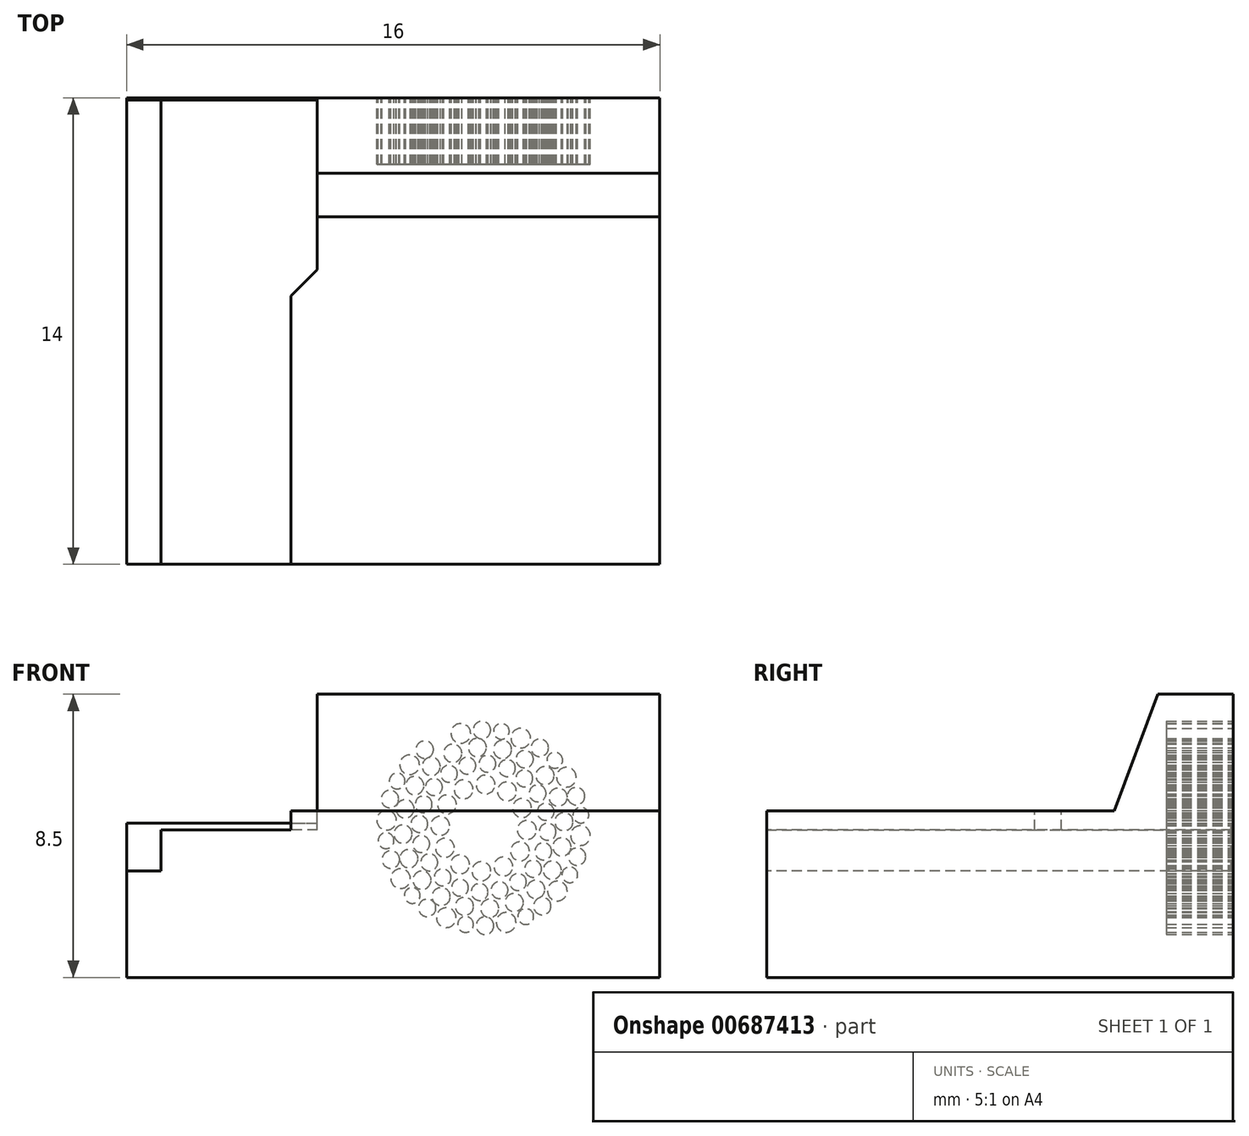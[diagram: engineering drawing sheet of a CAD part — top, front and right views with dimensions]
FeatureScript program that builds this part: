
annotation { "Feature Type Name" : "Feature", "Feature Type Description" : "" }
export const myFeature = defineFeature(function(context is Context, id is Id, definition is map)
    precondition{}
    {
        {
            var Q0;
            Q0=qCreatedBy(makeId("Top.planeOp"),FACE);
            var sketch = newSketch(context, id + "F0", { "sketchPlane" : qUnion([Q0])});
            skLineSegment(sketch, "E0.bottom", {"start": v(-4.9, 18.95) * mm, "end": v(-20.9, 18.95) * mm});
            skLineSegment(sketch, "E0.top", {"start": v(-4.9, 4.95) * mm, "end": v(-20.9, 4.95) * mm});
            skLineSegment(sketch, "E0.left", {"start": v(-4.9, 18.95) * mm, "end": v(-4.9, 4.95) * mm});
            skLineSegment(sketch, "E0.right", {"start": v(-20.9, 18.95) * mm, "end": v(-20.9, 4.95) * mm});
            skSolve(sketch);
        }
        {
            var Q0;
            Q0=makeQuery(id+"F0.imprint","IMPRINT",FACE,{"disambiguationData":[TD([[makeQuery(id+"F0.imprint","IMPRINT",EDGE,{"derivedFrom":sQuery(id+"F0.wireOp",EDGE,"E0.bottom")}),1.0]])]});
            extrude(context, id + "F1", {"entities" : qUnion([Q0]), "depth" : 5 * mm, "offsetDistance" : 25 * mm});
        }
        {
            var Q0;
            Q0=makeQuery(id+"F1.opExtrude","CAP_FACE",FACE,{"disambiguationData":[OSD([sQuery(id+"F0.wireOp",EDGE,"E0.bottom"),sQuery(id+"F0.wireOp",EDGE,"E0.top"),sQuery(id+"F0.wireOp",EDGE,"E0.left"),sQuery(id+"F0.wireOp",EDGE,"E0.right")])],"isStart":false});
            var sketch = newSketch(context, id + "F2", { "sketchPlane" : qUnion([Q0])});
            skLineSegment(sketch, "E1.bottom", {"start": v(-20.9, 18.95) * mm, "end": v(-19.87, 18.95) * mm});
            skLineSegment(sketch, "E1.right", {"start": v(-19.87, 18.95) * mm, "end": v(-19.87, 4.95) * mm});
            skSolve(sketch);
        }
        {
            var Q0;
            Q0=makeQuery(id+"F2.imprint","IMPRINT",FACE,{"disambiguationData":[TD([[makeQuery(id+"F2.imprint","IMPRINT",EDGE,{"derivedFrom":sQuery(id+"F2.wireOp",EDGE,"E1.bottom")}),1.0]])]});
            extrude(context, id + "F3", {"entities" : qUnion([Q0]), "operationType" : NewBodyOperationType.REMOVE, "oppositeDirection" : true, "depth" : 1.8 * mm, "offsetDistance" : 25 * mm});
        }
        {
            var Q0;
            Q0=makeQuery(id+"F1.opExtrude","CAP_FACE",FACE,{"disambiguationData":[OSD([sQuery(id+"F0.wireOp",EDGE,"E0.bottom"),sQuery(id+"F0.wireOp",EDGE,"E0.top"),sQuery(id+"F0.wireOp",EDGE,"E0.left"),sQuery(id+"F0.wireOp",EDGE,"E0.right")])],"isStart":false});
            var sketch = newSketch(context, id + "F4", { "sketchPlane" : qUnion([Q0])});
            skLineSegment(sketch, "E2", {"start": v(-19.87, 4.95) * mm, "end": v(-15.97, 4.95) * mm});
            skLineSegment(sketch, "E3", {"start": v(-15.97, 4.95) * mm, "end": v(-15.97, 13) * mm});
            skLineSegment(sketch, "E4", {"start": v(-15.97, 13) * mm, "end": v(-15.18, 13.8) * mm});
            skLineSegment(sketch, "E5", {"start": v(-15.18, 13.8) * mm, "end": v(-15.18, 18.95) * mm});
            skSolve(sketch);
        }
        {
            var Q0;
            Q0=makeQuery(id+"F4.imprint","IMPRINT",FACE,{"disambiguationData":[TD([[makeQuery(id+"F4.imprint","IMPRINT",EDGE,{"derivedFrom":sQuery(id+"F4.wireOp",EDGE,"E2")}),-1.0]])]});
            extrude(context, id + "F5", {"entities" : qUnion([Q0]), "operationType" : NewBodyOperationType.REMOVE, "oppositeDirection" : true, "depth" : 0.57 * mm, "offsetDistance" : 25 * mm});
        }
        {
            var Q0;
            Q0=makeQuery(id+"F1.opExtrude","CAP_FACE",FACE,{"disambiguationData":[OSD([sQuery(id+"F0.wireOp",EDGE,"E0.bottom"),sQuery(id+"F0.wireOp",EDGE,"E0.top"),sQuery(id+"F0.wireOp",EDGE,"E0.left"),sQuery(id+"F0.wireOp",EDGE,"E0.right")])],"isStart":false});
            var sketch = newSketch(context, id + "F6", { "sketchPlane" : qUnion([Q0])});
            skLineSegment(sketch, "E6.bottom", {"start": v(-4.9, 18.95) * mm, "end": v(-15.18, 18.95) * mm});
            skLineSegment(sketch, "E6.top", {"start": v(-4.9, 14.95) * mm, "end": v(-15.18, 14.95) * mm});
            skLineSegment(sketch, "E6.left", {"start": v(-4.9, 18.95) * mm, "end": v(-4.9, 14.95) * mm});
            skLineSegment(sketch, "E6.right", {"start": v(-15.18, 18.95) * mm, "end": v(-15.18, 14.95) * mm});
            skSolve(sketch);
        }
        {
            var Q0;
            Q0=makeQuery(id+"F6.imprint","IMPRINT",FACE,{"disambiguationData":[TD([[makeQuery(id+"F6.imprint","IMPRINT",EDGE,{"derivedFrom":sQuery(id+"F6.wireOp",EDGE,"E6.bottom")}),1.0]])]});
            extrude(context, id + "F7", {"entities" : qUnion([Q0]), "operationType" : NewBodyOperationType.ADD, "depth" : 3.5 * mm, "offsetDistance" : 25 * mm});
        }
        {
            var Q0;
            Q0=makeQuery(id+"F7.opExtrude","CAP_EDGE",EDGE,{"disambiguationData":[OSD([sQuery(id+"F6.wireOp",EDGE,"E6.top")])],"isStart":false});
            chamfer(context, id + "F8", {"entities" : qUnion([Q0]), "chamferType" : ChamferType.TWO_OFFSETS, "width1" : 4 * mm, "oppositeDirection" : false, "width2" : 1.5 * mm, "tangentPropagation" : true});
        }
        {
            var Q0;
            Q0=makeQuery(id+"F7.boolean.opBoolean","MERGE",FACE,{"derivedFrom":[makeQuery(id+"F1.opExtrude","SWEPT_FACE",FACE,{"disambiguationData":[OSD([sQuery(id+"F0.wireOp",EDGE,"E0.bottom")])]}),makeQuery(id+"F7.opExtrude","SWEPT_FACE",FACE,{"disambiguationData":[OSD([sQuery(id+"F6.wireOp",EDGE,"E6.bottom")])]})]});
            var sketch = newSketch(context, id + "F9", { "sketchPlane" : qUnion([Q0])});
            skLineSegment(sketch, "E7.bottom", {"start": v(20.9, 0) * mm, "end": v(15.18, 0) * mm});
            skLineSegment(sketch, "E7.top", {"start": v(20.9, 4.64) * mm, "end": v(15.18, 4.64) * mm});
            skLineSegment(sketch, "E7.left", {"start": v(20.9, 0) * mm, "end": v(20.9, 4.64) * mm});
            skLineSegment(sketch, "E7.right", {"start": v(15.18, 0) * mm, "end": v(15.18, 4.64) * mm});
            skSolve(sketch);
        }
        {
            var Q0;
            {var subQ3=sQuery(id+"F9.wireOp",EDGE,"E7.top");Q0=makeQuery(id+"F9.imprint","IMPRINT",FACE,{"disambiguationData":[TD([[makeQuery(id+"F9.imprint","IMPRINT",EDGE,{"derivedFrom":subQ3}),1.0]])]});}
            extrude(context, id + "F10", {"entities" : qUnion([Q0]), "operationType" : NewBodyOperationType.ADD, "oppositeDirection" : true, "depth" : 0.06 * mm, "offsetDistance" : 25 * mm});
        }
        {
            var Q0;
            {var subQ0=sQuery(id+"F0.wireOp",EDGE,"E0.bottom");Q0=makeQuery(id+"F10.boolean.opBoolean","MERGE",FACE,{"derivedFrom":[makeQuery(id+"F7.boolean.opBoolean","MERGE",FACE,{"derivedFrom":[makeQuery(id+"F1.opExtrude","SWEPT_FACE",FACE,{"disambiguationData":[OSD([subQ0])]}),makeQuery(id+"F7.opExtrude","SWEPT_FACE",FACE,{"disambiguationData":[OSD([sQuery(id+"F6.wireOp",EDGE,"E6.bottom")])]})]}),makeQuery(id+"F10.opExtrude","CAP_FACE",FACE,{"disambiguationData":[OSD([subQ0,sQuery(id+"F2.wireOp",EDGE,"E1.bottom"),sQuery(id+"F2.wireOp",EDGE,"E1.right"),sQuery(id+"F9.wireOp",EDGE,"E7.top"),sQuery(id+"F9.wireOp",EDGE,"E7.left"),sQuery(id+"F9.wireOp",EDGE,"E7.right")])],"isStart":true})]});}
            var sketch = newSketch(context, id + "F11", { "sketchPlane" : qUnion([Q0])});
            skLineSegment(sketch, "E8.0", {"start": v(9.14, 4.57) * mm, "end": v(9.59, 5.32) * mm});
            skLineSegment(sketch, "E8.1", {"start": v(9.73, 5.44) * mm, "end": v(10.61, 5.43) * mm});
            skLineSegment(sketch, "E8.2", {"start": v(10.79, 5.36) * mm, "end": v(11.21, 4.6) * mm});
            skLineSegment(sketch, "E8.3", {"start": v(11.25, 4.4) * mm, "end": v(10.8, 3.66) * mm});
            skLineSegment(sketch, "E8.4", {"start": v(10.65, 3.53) * mm, "end": v(9.77, 3.55) * mm});
            skLineSegment(sketch, "E8.5", {"start": v(9.6, 3.61) * mm, "end": v(9.17, 4.38) * mm});
            skPoint(sketch, "E8.0.midPoint", {"position": v(9.38, 4.98) * mm});
            skCircle(sketch, "E9", {"center": v(8.97, 5.98) * mm, "radius": 0.25 * mm});
            skCircle(sketch, "E10.1.0", {"center": v(8.57, 5.52) * mm, "radius": 0.25 * mm});
            skCircle(sketch, "E10.2.0", {"center": v(8.32, 4.97) * mm, "radius": 0.25 * mm});
            skPoint(sketch, "E10.center", {"position": v(10.2, 4.49) * mm});
            skCircle(sketch, "E11.1.3.0", {"center": v(8.27, 4.37) * mm, "radius": 0.25 * mm});
            skCircle(sketch, "E11.1.4.0", {"center": v(8.4, 3.78) * mm, "radius": 0.25 * mm});
            skCircle(sketch, "E11.1.5.0", {"center": v(8.7, 3.26) * mm, "radius": 0.25 * mm});
            skCircle(sketch, "E11.1.6.0", {"center": v(9.16, 2.86) * mm, "radius": 0.25 * mm});
            skCircle(sketch, "E11.1.7.0", {"center": v(9.7, 2.62) * mm, "radius": 0.25 * mm});
            skCircle(sketch, "E11.1.8.0", {"center": v(10.3, 2.56) * mm, "radius": 0.25 * mm});
            skCircle(sketch, "E11.1.9.0", {"center": v(10.9, 2.7) * mm, "radius": 0.25 * mm});
            skCircle(sketch, "E11.1.10.0", {"center": v(11.42, 3) * mm, "radius": 0.25 * mm});
            skCircle(sketch, "E11.1.11.0", {"center": v(11.82, 3.45) * mm, "radius": 0.25 * mm});
            skCircle(sketch, "E12.1.12.0", {"center": v(12.06, 4) * mm, "radius": 0.25 * mm});
            skCircle(sketch, "E13.1.13.0", {"center": v(12.12, 4.6) * mm, "radius": 0.25 * mm});
            skCircle(sketch, "E14.1.14.0", {"center": v(11.99, 5.2) * mm, "radius": 0.25 * mm});
            skCircle(sketch, "E14.1.15.0", {"center": v(11.68, 5.71) * mm, "radius": 0.25 * mm});
            skCircle(sketch, "E14.1.16.0", {"center": v(11.23, 6.11) * mm, "radius": 0.25 * mm});
            skCircle(sketch, "E14.1.17.0", {"center": v(10.67, 6.35) * mm, "radius": 0.25 * mm});
            skCircle(sketch, "E14.1.18.0", {"center": v(10.07, 6.41) * mm, "radius": 0.25 * mm});
            skCircle(sketch, "E14.1.19.0", {"center": v(9.49, 6.28) * mm, "radius": 0.25 * mm});
            skCircle(sketch, "E15", {"center": v(10.13, 5.79) * mm, "radius": 0.28 * mm});
            skCircle(sketch, "E16.1.0", {"center": v(9.49, 5.58) * mm, "radius": 0.28 * mm});
            skCircle(sketch, "E16.2.0", {"center": v(9.03, 5.08) * mm, "radius": 0.28 * mm});
            skCircle(sketch, "E16.3.0", {"center": v(8.9, 4.43) * mm, "radius": 0.28 * mm});
            skCircle(sketch, "E16.4.0", {"center": v(9.1, 3.78) * mm, "radius": 0.28 * mm});
            skCircle(sketch, "E16.5.0", {"center": v(9.6, 3.33) * mm, "radius": 0.28 * mm});
            skCircle(sketch, "E16.6.0", {"center": v(10.25, 3.19) * mm, "radius": 0.28 * mm});
            skCircle(sketch, "E16.7.0", {"center": v(10.9, 3.4) * mm, "radius": 0.28 * mm});
            skCircle(sketch, "E16.8.0", {"center": v(11.35, 3.9) * mm, "radius": 0.28 * mm});
            skCircle(sketch, "E16.9.0", {"center": v(11.5, 4.55) * mm, "radius": 0.28 * mm});
            skCircle(sketch, "E17.1.10.0", {"center": v(11.29, 5.2) * mm, "radius": 0.28 * mm});
            skCircle(sketch, "E18.1.11.0", {"center": v(10.79, 5.65) * mm, "radius": 0.28 * mm});
            skCircle(sketch, "E19", {"center": v(9.62, 6.84) * mm, "radius": 0.27 * mm});
            skCircle(sketch, "E20.2.0", {"center": v(8.35, 6.06) * mm, "radius": 0.27 * mm});
            skCircle(sketch, "E20.3.0", {"center": v(7.95, 5.4) * mm, "radius": 0.27 * mm});
            skCircle(sketch, "E20.4.0", {"center": v(7.78, 4.67) * mm, "radius": 0.27 * mm});
            skCircle(sketch, "E20.5.0", {"center": v(7.84, 3.92) * mm, "radius": 0.27 * mm});
            skCircle(sketch, "E20.6.0", {"center": v(8.13, 3.22) * mm, "radius": 0.27 * mm});
            skCircle(sketch, "E20.7.0", {"center": v(8.62, 2.64) * mm, "radius": 0.27 * mm});
            skCircle(sketch, "E20.8.0", {"center": v(9.27, 2.25) * mm, "radius": 0.27 * mm});
            skCircle(sketch, "E20.9.0", {"center": v(10, 2.07) * mm, "radius": 0.27 * mm});
            skCircle(sketch, "E21", {"center": v(8.95, 6.55) * mm, "radius": 0.26 * mm});
            skCircle(sketch, "E22.1.10.0", {"center": v(10.76, 2.13) * mm, "radius": 0.27 * mm});
            skCircle(sketch, "E22.1.11.0", {"center": v(11.46, 2.43) * mm, "radius": 0.27 * mm});
            skCircle(sketch, "E22.1.12.0", {"center": v(12.04, 2.92) * mm, "radius": 0.27 * mm});
            skCircle(sketch, "E22.1.13.0", {"center": v(12.43, 3.57) * mm, "radius": 0.27 * mm});
            skCircle(sketch, "E22.1.14.0", {"center": v(12.6, 4.3) * mm, "radius": 0.27 * mm});
            skCircle(sketch, "E22.1.15.0", {"center": v(12.55, 5.06) * mm, "radius": 0.27 * mm});
            skCircle(sketch, "E22.1.16.0", {"center": v(12.25, 5.76) * mm, "radius": 0.27 * mm});
            skCircle(sketch, "E22.1.17.0", {"center": v(11.76, 6.33) * mm, "radius": 0.27 * mm});
            skCircle(sketch, "E22.1.18.0", {"center": v(11.11, 6.73) * mm, "radius": 0.27 * mm});
            skCircle(sketch, "E22.1.19.0", {"center": v(10.38, 6.9) * mm, "radius": 0.27 * mm});
            skCircle(sketch, "E23", {"center": v(9.07, 7.18) * mm, "radius": 0.3 * mm});
            skCircle(sketch, "E24.1.0", {"center": v(7.7, 6.01) * mm, "radius": 0.3 * mm});
            skCircle(sketch, "E24.2.0", {"center": v(7.28, 4.26) * mm, "radius": 0.3 * mm});
            skCircle(sketch, "E24.3.0", {"center": v(7.98, 2.6) * mm, "radius": 0.3 * mm});
            skCircle(sketch, "E24.4.0", {"center": v(9.51, 1.65) * mm, "radius": 0.3 * mm});
            skCircle(sketch, "E24.5.0", {"center": v(11.3, 1.8) * mm, "radius": 0.3 * mm});
            skCircle(sketch, "E24.6.0", {"center": v(12.68, 2.97) * mm, "radius": 0.3 * mm});
            skCircle(sketch, "E24.7.0", {"center": v(13.1, 4.72) * mm, "radius": 0.3 * mm});
            skCircle(sketch, "E24.8.0", {"center": v(12.4, 6.38) * mm, "radius": 0.3 * mm});
            skCircle(sketch, "E24.9.0", {"center": v(10.87, 7.32) * mm, "radius": 0.3 * mm});
            skCircle(sketch, "E25", {"center": v(8.5, 6.9) * mm, "radius": 0.26 * mm});
            skCircle(sketch, "E26.1.0", {"center": v(7.41, 5.44) * mm, "radius": 0.26 * mm});
            skCircle(sketch, "E26.2.0", {"center": v(7.38, 3.62) * mm, "radius": 0.26 * mm});
            skCircle(sketch, "E26.3.0", {"center": v(8.43, 2.14) * mm, "radius": 0.26 * mm});
            skCircle(sketch, "E26.4.0", {"center": v(10.15, 1.55) * mm, "radius": 0.26 * mm});
            skCircle(sketch, "E26.5.0", {"center": v(11.88, 2.09) * mm, "radius": 0.26 * mm});
            skCircle(sketch, "E26.6.0", {"center": v(12.97, 3.54) * mm, "radius": 0.26 * mm});
            skCircle(sketch, "E26.7.0", {"center": v(13, 5.35) * mm, "radius": 0.26 * mm});
            skCircle(sketch, "E26.8.0", {"center": v(11.95, 6.84) * mm, "radius": 0.26 * mm});
            skCircle(sketch, "E26.9.0", {"center": v(10.24, 7.42) * mm, "radius": 0.26 * mm});
            skCircle(sketch, "E27", {"center": v(8.05, 6.52) * mm, "radius": 0.24 * mm});
            skCircle(sketch, "E28.1.0", {"center": v(7.27, 4.87) * mm, "radius": 0.24 * mm});
            skCircle(sketch, "E28.2.0", {"center": v(7.6, 3.08) * mm, "radius": 0.24 * mm});
            skCircle(sketch, "E28.3.0", {"center": v(8.92, 1.83) * mm, "radius": 0.24 * mm});
            skCircle(sketch, "E28.4.0", {"center": v(10.73, 1.59) * mm, "radius": 0.24 * mm});
            skCircle(sketch, "E28.5.0", {"center": v(12.33, 2.46) * mm, "radius": 0.24 * mm});
            skCircle(sketch, "E28.6.0", {"center": v(13.11, 4.1) * mm, "radius": 0.24 * mm});
            skCircle(sketch, "E28.7.0", {"center": v(12.78, 5.9) * mm, "radius": 0.24 * mm});
            skCircle(sketch, "E28.8.0", {"center": v(11.46, 7.15) * mm, "radius": 0.24 * mm});
            skCircle(sketch, "E28.9.0", {"center": v(9.65, 7.39) * mm, "radius": 0.24 * mm});
            skPoint(sketch, "E29.orphan", {"position": v(9.1, 4.5) * mm});
            skPoint(sketch, "E30.orphan", {"position": v(9.66, 5.44) * mm});
            skPoint(sketch, "E31.orphan", {"position": v(10.76, 5.42) * mm});
            skPoint(sketch, "E32.orphan", {"position": v(11.28, 4.47) * mm});
            skPoint(sketch, "E33.orphan", {"position": v(9.63, 3.55) * mm});
            skLineSegment(sketch, "E34", {"start": v(7.18, 7.97) * mm, "end": v(13.02, 7.97) * mm});
            skLineSegment(sketch, "E35", {"start": v(13.65, 7.4) * mm, "end": v(13.65, 1.67) * mm});
            skLineSegment(sketch, "E36", {"start": v(13.14, 1.14) * mm, "end": v(7.3, 1.14) * mm});
            skLineSegment(sketch, "E37", {"start": v(6.72, 1.66) * mm, "end": v(6.75, 7.43) * mm});
            skLineSegment(sketch, "E38", {"start": v(6.75, 7.43) * mm, "end": v(7.18, 7.97) * mm});
            skLineSegment(sketch, "E39", {"start": v(13.02, 7.97) * mm, "end": v(13.65, 7.4) * mm});
            skLineSegment(sketch, "E40", {"start": v(13.65, 1.67) * mm, "end": v(13.14, 1.14) * mm});
            skLineSegment(sketch, "E41", {"start": v(6.72, 1.66) * mm, "end": v(7.3, 1.14) * mm});
            skSolve(sketch);
        }
        {
            var Q0;
            Q0=makeQuery(id+"F11.imprint","IMPRINT",FACE,{"disambiguationData":[TD([[makeQuery(id+"F11.imprint","IMPRINT",EDGE,{"derivedFrom":sQuery(id+"F11.wireOp",EDGE,"E25")}),1.0]])]});
            var Q1;
            Q1=makeQuery(id+"F11.imprint","IMPRINT",FACE,{"disambiguationData":[TD([[makeQuery(id+"F11.imprint","IMPRINT",EDGE,{"derivedFrom":sQuery(id+"F11.wireOp",EDGE,"E23")}),1.0]])]});
            var Q2;
            Q2=makeQuery(id+"F11.imprint","IMPRINT",FACE,{"disambiguationData":[TD([[makeQuery(id+"F11.imprint","IMPRINT",EDGE,{"derivedFrom":sQuery(id+"F11.wireOp",EDGE,"E28.9.0")}),1.0]])]});
            var Q3;
            Q3=makeQuery(id+"F11.imprint","IMPRINT",FACE,{"disambiguationData":[TD([[makeQuery(id+"F11.imprint","IMPRINT",EDGE,{"derivedFrom":sQuery(id+"F11.wireOp",EDGE,"E26.9.0")}),1.0]])]});
            var Q4;
            Q4=makeQuery(id+"F11.imprint","IMPRINT",FACE,{"disambiguationData":[TD([[makeQuery(id+"F11.imprint","IMPRINT",EDGE,{"derivedFrom":sQuery(id+"F11.wireOp",EDGE,"E24.9.0")}),1.0]])]});
            var Q5;
            Q5=makeQuery(id+"F11.imprint","IMPRINT",FACE,{"disambiguationData":[TD([[makeQuery(id+"F11.imprint","IMPRINT",EDGE,{"derivedFrom":sQuery(id+"F11.wireOp",EDGE,"E24.8.0")}),1.0]])]});
            var Q6;
            Q6=makeQuery(id+"F11.imprint","IMPRINT",FACE,{"disambiguationData":[TD([[makeQuery(id+"F11.imprint","IMPRINT",EDGE,{"derivedFrom":sQuery(id+"F11.wireOp",EDGE,"E22.1.17.0")}),1.0]])]});
            var Q7;
            Q7=makeQuery(id+"F11.imprint","IMPRINT",FACE,{"disambiguationData":[TD([[makeQuery(id+"F11.imprint","IMPRINT",EDGE,{"derivedFrom":sQuery(id+"F11.wireOp",EDGE,"E22.1.16.0")}),1.0]])]});
            var Q8;
            Q8=makeQuery(id+"F11.imprint","IMPRINT",FACE,{"disambiguationData":[TD([[makeQuery(id+"F11.imprint","IMPRINT",EDGE,{"derivedFrom":sQuery(id+"F11.wireOp",EDGE,"E28.7.0")}),1.0]])]});
            var Q9;
            Q9=makeQuery(id+"F11.imprint","IMPRINT",FACE,{"disambiguationData":[TD([[makeQuery(id+"F11.imprint","IMPRINT",EDGE,{"derivedFrom":sQuery(id+"F11.wireOp",EDGE,"E26.7.0")}),1.0]])]});
            var Q10;
            Q10=makeQuery(id+"F11.imprint","IMPRINT",FACE,{"disambiguationData":[TD([[makeQuery(id+"F11.imprint","IMPRINT",EDGE,{"derivedFrom":sQuery(id+"F11.wireOp",EDGE,"E22.1.15.0")}),1.0]])]});
            var Q11;
            Q11=makeQuery(id+"F11.imprint","IMPRINT",FACE,{"disambiguationData":[TD([[makeQuery(id+"F11.imprint","IMPRINT",EDGE,{"derivedFrom":sQuery(id+"F11.wireOp",EDGE,"E14.1.14.0")}),1.0]])]});
            var Q12;
            Q12=makeQuery(id+"F11.imprint","IMPRINT",FACE,{"disambiguationData":[TD([[makeQuery(id+"F11.imprint","IMPRINT",EDGE,{"derivedFrom":sQuery(id+"F11.wireOp",EDGE,"E14.1.15.0")}),1.0]])]});
            var Q13;
            Q13=makeQuery(id+"F11.imprint","IMPRINT",FACE,{"disambiguationData":[TD([[makeQuery(id+"F11.imprint","IMPRINT",EDGE,{"derivedFrom":sQuery(id+"F11.wireOp",EDGE,"E14.1.16.0")}),1.0]])]});
            var Q14;
            Q14=makeQuery(id+"F11.imprint","IMPRINT",FACE,{"disambiguationData":[TD([[makeQuery(id+"F11.imprint","IMPRINT",EDGE,{"derivedFrom":sQuery(id+"F11.wireOp",EDGE,"E22.1.19.0")}),1.0]])]});
            var Q15;
            Q15=makeQuery(id+"F11.imprint","IMPRINT",FACE,{"disambiguationData":[TD([[makeQuery(id+"F11.imprint","IMPRINT",EDGE,{"derivedFrom":sQuery(id+"F11.wireOp",EDGE,"E14.1.17.0")}),1.0]])]});
            var Q16;
            Q16=makeQuery(id+"F11.imprint","IMPRINT",FACE,{"disambiguationData":[TD([[makeQuery(id+"F11.imprint","IMPRINT",EDGE,{"derivedFrom":sQuery(id+"F11.wireOp",EDGE,"E14.1.18.0")}),1.0]])]});
            var Q17;
            Q17=makeQuery(id+"F11.imprint","IMPRINT",FACE,{"disambiguationData":[TD([[makeQuery(id+"F11.imprint","IMPRINT",EDGE,{"derivedFrom":sQuery(id+"F11.wireOp",EDGE,"E19")}),1.0]])]});
            var Q18;
            Q18=makeQuery(id+"F11.imprint","IMPRINT",FACE,{"disambiguationData":[TD([[makeQuery(id+"F11.imprint","IMPRINT",EDGE,{"derivedFrom":sQuery(id+"F11.wireOp",EDGE,"E14.1.19.0")}),1.0]])]});
            var Q19;
            {var subQ0=sQuery(id+"F11.wireOp",EDGE,"E16.1.0");var subQ1=makeQuery(id+"F11.imprint","INTERSECT",VERTEX,{"derivedFrom":[sQuery(id+"F11.wireOp",EDGE,"E8.0"),subQ0]});Q19=makeQuery(id+"F11.imprint","IMPRINT",FACE,{"disambiguationData":[TD([[makeQuery(id+"F11.imprint","IMPRINT",EDGE,{"disambiguationData":[TD([[subQ1,-1.0]])],"derivedFrom":subQ0}),1.0]])]});}
            var Q20;
            Q20=makeQuery(id+"F11.imprint","IMPRINT",FACE,{"disambiguationData":[TD([[makeQuery(id+"F11.imprint","IMPRINT",EDGE,{"derivedFrom":sQuery(id+"F11.wireOp",EDGE,"E15")}),1.0]])]});
            var Q21;
            {var subQ0=sQuery(id+"F11.wireOp",EDGE,"E18.1.11.0");var subQ1=makeQuery(id+"F11.imprint","INTERSECT",VERTEX,{"derivedFrom":[sQuery(id+"F11.wireOp",EDGE,"E8.1"),subQ0]});Q21=makeQuery(id+"F11.imprint","IMPRINT",FACE,{"disambiguationData":[TD([[makeQuery(id+"F11.imprint","IMPRINT",EDGE,{"disambiguationData":[TD([[subQ1,-1.0]])],"derivedFrom":subQ0}),1.0]])]});}
            var Q22;
            Q22=makeQuery(id+"F11.imprint","IMPRINT",FACE,{"disambiguationData":[TD([[makeQuery(id+"F11.imprint","IMPRINT",EDGE,{"derivedFrom":sQuery(id+"F11.wireOp",EDGE,"E22.1.18.0")}),1.0]])]});
            var Q23;
            Q23=makeQuery(id+"F11.imprint","IMPRINT",FACE,{"disambiguationData":[TD([[makeQuery(id+"F11.imprint","IMPRINT",EDGE,{"derivedFrom":sQuery(id+"F11.wireOp",EDGE,"E17.1.10.0")}),1.0]])]});
            var Q24;
            {var subQ0=sQuery(id+"F11.wireOp",EDGE,"E16.9.0");var subQ1=makeQuery(id+"F11.imprint","INTERSECT",VERTEX,{"derivedFrom":[sQuery(id+"F11.wireOp",EDGE,"E8.2"),subQ0]});Q24=makeQuery(id+"F11.imprint","IMPRINT",FACE,{"disambiguationData":[TD([[makeQuery(id+"F11.imprint","IMPRINT",EDGE,{"disambiguationData":[TD([[subQ1,-1.0]])],"derivedFrom":subQ0}),1.0]])]});}
            var Q25;
            Q25=makeQuery(id+"F11.imprint","IMPRINT",FACE,{"disambiguationData":[TD([[makeQuery(id+"F11.imprint","IMPRINT",EDGE,{"derivedFrom":sQuery(id+"F11.wireOp",EDGE,"E13.1.13.0")}),1.0]])]});
            var Q26;
            Q26=makeQuery(id+"F11.imprint","IMPRINT",FACE,{"disambiguationData":[TD([[makeQuery(id+"F11.imprint","IMPRINT",EDGE,{"derivedFrom":sQuery(id+"F11.wireOp",EDGE,"E22.1.14.0")}),1.0]])]});
            var Q27;
            Q27=makeQuery(id+"F11.imprint","IMPRINT",FACE,{"disambiguationData":[TD([[makeQuery(id+"F11.imprint","IMPRINT",EDGE,{"derivedFrom":sQuery(id+"F11.wireOp",EDGE,"E24.7.0")}),1.0]])]});
            var Q28;
            Q28=makeQuery(id+"F11.imprint","IMPRINT",FACE,{"disambiguationData":[TD([[makeQuery(id+"F11.imprint","IMPRINT",EDGE,{"derivedFrom":sQuery(id+"F11.wireOp",EDGE,"E28.6.0")}),1.0]])]});
            var Q29;
            Q29=makeQuery(id+"F11.imprint","IMPRINT",FACE,{"disambiguationData":[TD([[makeQuery(id+"F11.imprint","IMPRINT",EDGE,{"derivedFrom":sQuery(id+"F11.wireOp",EDGE,"E26.6.0")}),1.0]])]});
            var Q30;
            Q30=makeQuery(id+"F11.imprint","IMPRINT",FACE,{"disambiguationData":[TD([[makeQuery(id+"F11.imprint","IMPRINT",EDGE,{"derivedFrom":sQuery(id+"F11.wireOp",EDGE,"E22.1.13.0")}),1.0]])]});
            var Q31;
            Q31=makeQuery(id+"F11.imprint","IMPRINT",FACE,{"disambiguationData":[TD([[makeQuery(id+"F11.imprint","IMPRINT",EDGE,{"derivedFrom":sQuery(id+"F11.wireOp",EDGE,"E12.1.12.0")}),1.0]])]});
            var Q32;
            Q32=makeQuery(id+"F11.imprint","IMPRINT",FACE,{"disambiguationData":[TD([[makeQuery(id+"F11.imprint","IMPRINT",EDGE,{"derivedFrom":sQuery(id+"F11.wireOp",EDGE,"E11.1.11.0")}),1.0]])]});
            var Q33;
            Q33=makeQuery(id+"F11.imprint","IMPRINT",FACE,{"disambiguationData":[TD([[makeQuery(id+"F11.imprint","IMPRINT",EDGE,{"derivedFrom":sQuery(id+"F11.wireOp",EDGE,"E16.8.0")}),1.0]])]});
            var Q34;
            {var subQ0=sQuery(id+"F11.wireOp",EDGE,"E16.7.0");var subQ1=makeQuery(id+"F11.imprint","INTERSECT",VERTEX,{"derivedFrom":[sQuery(id+"F11.wireOp",EDGE,"E8.3"),subQ0]});Q34=makeQuery(id+"F11.imprint","IMPRINT",FACE,{"disambiguationData":[TD([[makeQuery(id+"F11.imprint","IMPRINT",EDGE,{"disambiguationData":[TD([[subQ1,-1.0]])],"derivedFrom":subQ0}),1.0]])]});}
            var Q35;
            Q35=makeQuery(id+"F11.imprint","IMPRINT",FACE,{"disambiguationData":[TD([[makeQuery(id+"F11.imprint","IMPRINT",EDGE,{"derivedFrom":sQuery(id+"F11.wireOp",EDGE,"E16.2.0")}),1.0]])]});
            var Q36;
            Q36=makeQuery(id+"F11.imprint","IMPRINT",FACE,{"disambiguationData":[TD([[makeQuery(id+"F11.imprint","IMPRINT",EDGE,{"derivedFrom":sQuery(id+"F11.wireOp",EDGE,"E9")}),1.0]])]});
            var Q37;
            Q37=makeQuery(id+"F11.imprint","IMPRINT",FACE,{"disambiguationData":[TD([[makeQuery(id+"F11.imprint","IMPRINT",EDGE,{"derivedFrom":sQuery(id+"F11.wireOp",EDGE,"E21")}),1.0]])]});
            var Q38;
            Q38=makeQuery(id+"F11.imprint","IMPRINT",FACE,{"disambiguationData":[TD([[makeQuery(id+"F11.imprint","IMPRINT",EDGE,{"derivedFrom":sQuery(id+"F11.wireOp",EDGE,"E20.2.0")}),1.0]])]});
            var Q39;
            Q39=makeQuery(id+"F11.imprint","IMPRINT",FACE,{"disambiguationData":[TD([[makeQuery(id+"F11.imprint","IMPRINT",EDGE,{"derivedFrom":sQuery(id+"F11.wireOp",EDGE,"E27")}),1.0]])]});
            var Q40;
            Q40=makeQuery(id+"F11.imprint","IMPRINT",FACE,{"disambiguationData":[TD([[makeQuery(id+"F11.imprint","IMPRINT",EDGE,{"derivedFrom":sQuery(id+"F11.wireOp",EDGE,"E24.1.0")}),1.0]])]});
            var Q41;
            Q41=makeQuery(id+"F11.imprint","IMPRINT",FACE,{"disambiguationData":[TD([[makeQuery(id+"F11.imprint","IMPRINT",EDGE,{"derivedFrom":sQuery(id+"F11.wireOp",EDGE,"E20.3.0")}),1.0]])]});
            var Q42;
            Q42=makeQuery(id+"F11.imprint","IMPRINT",FACE,{"disambiguationData":[TD([[makeQuery(id+"F11.imprint","IMPRINT",EDGE,{"derivedFrom":sQuery(id+"F11.wireOp",EDGE,"E10.1.0")}),1.0]])]});
            var Q43;
            Q43=makeQuery(id+"F11.imprint","IMPRINT",FACE,{"disambiguationData":[TD([[makeQuery(id+"F11.imprint","IMPRINT",EDGE,{"derivedFrom":sQuery(id+"F11.wireOp",EDGE,"E10.2.0")}),1.0]])]});
            var Q44;
            {var subQ0=sQuery(id+"F11.wireOp",EDGE,"E16.3.0");var subQ1=makeQuery(id+"F11.imprint","INTERSECT",VERTEX,{"derivedFrom":[sQuery(id+"F11.wireOp",EDGE,"E8.0"),subQ0]});Q44=makeQuery(id+"F11.imprint","IMPRINT",FACE,{"disambiguationData":[TD([[makeQuery(id+"F11.imprint","IMPRINT",EDGE,{"disambiguationData":[TD([[subQ1,1.0]])],"derivedFrom":subQ0}),1.0]])]});}
            var Q45;
            Q45=makeQuery(id+"F11.imprint","IMPRINT",FACE,{"disambiguationData":[TD([[makeQuery(id+"F11.imprint","IMPRINT",EDGE,{"derivedFrom":sQuery(id+"F11.wireOp",EDGE,"E11.1.3.0")}),1.0]])]});
            var Q46;
            Q46=makeQuery(id+"F11.imprint","IMPRINT",FACE,{"disambiguationData":[TD([[makeQuery(id+"F11.imprint","IMPRINT",EDGE,{"derivedFrom":sQuery(id+"F11.wireOp",EDGE,"E20.4.0")}),1.0]])]});
            var Q47;
            Q47=makeQuery(id+"F11.imprint","IMPRINT",FACE,{"disambiguationData":[TD([[makeQuery(id+"F11.imprint","IMPRINT",EDGE,{"derivedFrom":sQuery(id+"F11.wireOp",EDGE,"E28.1.0")}),1.0]])]});
            var Q48;
            Q48=makeQuery(id+"F11.imprint","IMPRINT",FACE,{"disambiguationData":[TD([[makeQuery(id+"F11.imprint","IMPRINT",EDGE,{"derivedFrom":sQuery(id+"F11.wireOp",EDGE,"E26.1.0")}),1.0]])]});
            var Q49;
            Q49=makeQuery(id+"F11.imprint","IMPRINT",FACE,{"disambiguationData":[TD([[makeQuery(id+"F11.imprint","IMPRINT",EDGE,{"derivedFrom":sQuery(id+"F11.wireOp",EDGE,"E24.2.0")}),1.0]])]});
            var Q50;
            Q50=makeQuery(id+"F11.imprint","IMPRINT",FACE,{"disambiguationData":[TD([[makeQuery(id+"F11.imprint","IMPRINT",EDGE,{"derivedFrom":sQuery(id+"F11.wireOp",EDGE,"E26.2.0")}),1.0]])]});
            var Q51;
            Q51=makeQuery(id+"F11.imprint","IMPRINT",FACE,{"disambiguationData":[TD([[makeQuery(id+"F11.imprint","IMPRINT",EDGE,{"derivedFrom":sQuery(id+"F11.wireOp",EDGE,"E20.5.0")}),1.0]])]});
            var Q52;
            Q52=makeQuery(id+"F11.imprint","IMPRINT",FACE,{"disambiguationData":[TD([[makeQuery(id+"F11.imprint","IMPRINT",EDGE,{"derivedFrom":sQuery(id+"F11.wireOp",EDGE,"E11.1.4.0")}),1.0]])]});
            var Q53;
            Q53=makeQuery(id+"F11.imprint","IMPRINT",FACE,{"disambiguationData":[TD([[makeQuery(id+"F11.imprint","IMPRINT",EDGE,{"derivedFrom":sQuery(id+"F11.wireOp",EDGE,"E16.4.0")}),1.0]])]});
            var Q54;
            Q54=makeQuery(id+"F11.imprint","IMPRINT",FACE,{"disambiguationData":[TD([[makeQuery(id+"F11.imprint","IMPRINT",EDGE,{"derivedFrom":sQuery(id+"F11.wireOp",EDGE,"E20.8.0")}),1.0]])]});
            var Q55;
            Q55=makeQuery(id+"F11.imprint","IMPRINT",FACE,{"disambiguationData":[TD([[makeQuery(id+"F11.imprint","IMPRINT",EDGE,{"derivedFrom":sQuery(id+"F11.wireOp",EDGE,"E16.6.0")}),1.0]])]});
            var Q56;
            Q56=makeQuery(id+"F11.imprint","IMPRINT",FACE,{"disambiguationData":[TD([[makeQuery(id+"F11.imprint","IMPRINT",EDGE,{"derivedFrom":sQuery(id+"F11.wireOp",EDGE,"E11.1.8.0")}),1.0]])]});
            var Q57;
            Q57=makeQuery(id+"F11.imprint","IMPRINT",FACE,{"disambiguationData":[TD([[makeQuery(id+"F11.imprint","IMPRINT",EDGE,{"derivedFrom":sQuery(id+"F11.wireOp",EDGE,"E11.1.7.0")}),1.0]])]});
            var Q58;
            Q58=makeQuery(id+"F11.imprint","IMPRINT",FACE,{"disambiguationData":[TD([[makeQuery(id+"F11.imprint","IMPRINT",EDGE,{"derivedFrom":sQuery(id+"F11.wireOp",EDGE,"E20.9.0")}),1.0]])]});
            var Q59;
            Q59=makeQuery(id+"F11.imprint","IMPRINT",FACE,{"disambiguationData":[TD([[makeQuery(id+"F11.imprint","IMPRINT",EDGE,{"derivedFrom":sQuery(id+"F11.wireOp",EDGE,"E26.4.0")}),1.0]])]});
            var Q60;
            Q60=makeQuery(id+"F11.imprint","IMPRINT",FACE,{"disambiguationData":[TD([[makeQuery(id+"F11.imprint","IMPRINT",EDGE,{"derivedFrom":sQuery(id+"F11.wireOp",EDGE,"E24.4.0")}),1.0]])]});
            var Q61;
            Q61=makeQuery(id+"F11.imprint","IMPRINT",FACE,{"disambiguationData":[TD([[makeQuery(id+"F11.imprint","IMPRINT",EDGE,{"derivedFrom":sQuery(id+"F11.wireOp",EDGE,"E28.4.0")}),1.0]])]});
            var Q62;
            Q62=makeQuery(id+"F11.imprint","IMPRINT",FACE,{"disambiguationData":[TD([[makeQuery(id+"F11.imprint","IMPRINT",EDGE,{"derivedFrom":sQuery(id+"F11.wireOp",EDGE,"E11.1.9.0")}),1.0]])]});
            var Q63;
            Q63=makeQuery(id+"F11.imprint","IMPRINT",FACE,{"disambiguationData":[TD([[makeQuery(id+"F11.imprint","IMPRINT",EDGE,{"derivedFrom":sQuery(id+"F11.wireOp",EDGE,"E11.1.10.0")}),1.0]])]});
            var Q64;
            Q64=makeQuery(id+"F11.imprint","IMPRINT",FACE,{"disambiguationData":[TD([[makeQuery(id+"F11.imprint","IMPRINT",EDGE,{"derivedFrom":sQuery(id+"F11.wireOp",EDGE,"E22.1.10.0")}),1.0]])]});
            var Q65;
            Q65=makeQuery(id+"F11.imprint","IMPRINT",FACE,{"disambiguationData":[TD([[makeQuery(id+"F11.imprint","IMPRINT",EDGE,{"derivedFrom":sQuery(id+"F11.wireOp",EDGE,"E24.5.0")}),1.0]])]});
            var Q66;
            Q66=makeQuery(id+"F11.imprint","IMPRINT",FACE,{"disambiguationData":[TD([[makeQuery(id+"F11.imprint","IMPRINT",EDGE,{"derivedFrom":sQuery(id+"F11.wireOp",EDGE,"E22.1.11.0")}),1.0]])]});
            var Q67;
            Q67=makeQuery(id+"F11.imprint","IMPRINT",FACE,{"disambiguationData":[TD([[makeQuery(id+"F11.imprint","IMPRINT",EDGE,{"derivedFrom":sQuery(id+"F11.wireOp",EDGE,"E22.1.12.0")}),1.0]])]});
            var Q68;
            Q68=makeQuery(id+"F11.imprint","IMPRINT",FACE,{"disambiguationData":[TD([[makeQuery(id+"F11.imprint","IMPRINT",EDGE,{"derivedFrom":sQuery(id+"F11.wireOp",EDGE,"E24.6.0")}),1.0]])]});
            var Q69;
            Q69=makeQuery(id+"F11.imprint","IMPRINT",FACE,{"disambiguationData":[TD([[makeQuery(id+"F11.imprint","IMPRINT",EDGE,{"derivedFrom":sQuery(id+"F11.wireOp",EDGE,"E28.5.0")}),1.0]])]});
            var Q70;
            Q70=makeQuery(id+"F11.imprint","IMPRINT",FACE,{"disambiguationData":[TD([[makeQuery(id+"F11.imprint","IMPRINT",EDGE,{"derivedFrom":sQuery(id+"F11.wireOp",EDGE,"E26.5.0")}),1.0]])]});
            var Q71;
            Q71=makeQuery(id+"F11.imprint","IMPRINT",FACE,{"disambiguationData":[TD([[makeQuery(id+"F11.imprint","IMPRINT",EDGE,{"derivedFrom":sQuery(id+"F11.wireOp",EDGE,"E11.1.6.0")}),1.0]])]});
            var Q72;
            {var subQ0=sQuery(id+"F11.wireOp",EDGE,"E16.5.0");var subQ1=makeQuery(id+"F11.imprint","INTERSECT",VERTEX,{"derivedFrom":[sQuery(id+"F11.wireOp",EDGE,"E8.4"),subQ0]});Q72=makeQuery(id+"F11.imprint","IMPRINT",FACE,{"disambiguationData":[TD([[makeQuery(id+"F11.imprint","IMPRINT",EDGE,{"disambiguationData":[TD([[subQ1,-1.0]])],"derivedFrom":subQ0}),1.0]])]});}
            var Q73;
            Q73=makeQuery(id+"F11.imprint","IMPRINT",FACE,{"disambiguationData":[TD([[makeQuery(id+"F11.imprint","IMPRINT",EDGE,{"derivedFrom":sQuery(id+"F11.wireOp",EDGE,"E11.1.5.0")}),1.0]])]});
            var Q74;
            Q74=makeQuery(id+"F11.imprint","IMPRINT",FACE,{"disambiguationData":[TD([[makeQuery(id+"F11.imprint","IMPRINT",EDGE,{"derivedFrom":sQuery(id+"F11.wireOp",EDGE,"E20.7.0")}),1.0]])]});
            var Q75;
            Q75=makeQuery(id+"F11.imprint","IMPRINT",FACE,{"disambiguationData":[TD([[makeQuery(id+"F11.imprint","IMPRINT",EDGE,{"derivedFrom":sQuery(id+"F11.wireOp",EDGE,"E24.3.0")}),1.0]])]});
            var Q76;
            Q76=makeQuery(id+"F11.imprint","IMPRINT",FACE,{"disambiguationData":[TD([[makeQuery(id+"F11.imprint","IMPRINT",EDGE,{"derivedFrom":sQuery(id+"F11.wireOp",EDGE,"E26.3.0")}),1.0]])]});
            var Q77;
            Q77=makeQuery(id+"F11.imprint","IMPRINT",FACE,{"disambiguationData":[TD([[makeQuery(id+"F11.imprint","IMPRINT",EDGE,{"derivedFrom":sQuery(id+"F11.wireOp",EDGE,"E28.3.0")}),1.0]])]});
            var Q78;
            Q78=makeQuery(id+"F11.imprint","IMPRINT",FACE,{"disambiguationData":[TD([[makeQuery(id+"F11.imprint","IMPRINT",EDGE,{"derivedFrom":sQuery(id+"F11.wireOp",EDGE,"E28.2.0")}),1.0]])]});
            var Q79;
            Q79=makeQuery(id+"F11.imprint","IMPRINT",FACE,{"disambiguationData":[TD([[makeQuery(id+"F11.imprint","IMPRINT",EDGE,{"derivedFrom":sQuery(id+"F11.wireOp",EDGE,"E20.6.0")}),1.0]])]});
            var Q80;
            Q80=makeQuery(id+"F11.imprint","IMPRINT",FACE,{"disambiguationData":[TD([[makeQuery(id+"F11.imprint","IMPRINT",EDGE,{"derivedFrom":sQuery(id+"F11.wireOp",EDGE,"E26.8.0")}),1.0]])]});
            extrude(context, id + "F12", {"entities" : qUnion([Q0, Q1, Q2, Q3, Q4, Q5, Q6, Q7, Q8, Q9, Q10, Q11, Q12, Q13, Q14, Q15, Q16, Q17, Q18, Q19, Q20, Q21, Q22, Q23, Q24, Q25, Q26, Q27, Q28, Q29, Q30, Q31, Q32, Q33, Q34, Q35, Q36, Q37, Q38, Q39, Q40, Q41, Q42, Q43, Q44, Q45, Q46, Q47, Q48, Q49, Q50, Q51, Q52, Q53, Q54, Q55, Q56, Q57, Q58, Q59, Q60, Q61, Q62, Q63, Q64, Q65, Q66, Q67, Q68, Q69, Q70, Q71, Q72, Q73, Q74, Q75, Q76, Q77, Q78, Q79, Q80]), "operationType" : NewBodyOperationType.REMOVE, "oppositeDirection" : true, "depth" : 2 * mm, "offsetDistance" : 25 * mm});
        }
        {
            var Q0;
            Q0=makeQuery(id+"F11.imprint","IMPRINT",FACE,{"disambiguationData":[TD([[makeQuery(id+"F11.imprint","IMPRINT",EDGE,{"derivedFrom":sQuery(id+"F11.wireOp",EDGE,"E26.9.0")}),1.0]])]});
            var Q1;
            Q1=makeQuery(id+"F11.imprint","IMPRINT",FACE,{"disambiguationData":[TD([[makeQuery(id+"F11.imprint","IMPRINT",EDGE,{"derivedFrom":sQuery(id+"F11.wireOp",EDGE,"E22.1.19.0")}),1.0]])]});
            var Q2;
            Q2=makeQuery(id+"F11.imprint","IMPRINT",FACE,{"disambiguationData":[TD([[makeQuery(id+"F11.imprint","IMPRINT",EDGE,{"derivedFrom":sQuery(id+"F11.wireOp",EDGE,"E24.9.0")}),1.0]])]});
            var Q3;
            Q3=makeQuery(id+"F11.imprint","IMPRINT",FACE,{"disambiguationData":[TD([[makeQuery(id+"F11.imprint","IMPRINT",EDGE,{"derivedFrom":sQuery(id+"F11.wireOp",EDGE,"E28.8.0")}),1.0]])]});
            var Q4;
            Q4=makeQuery(id+"F11.imprint","IMPRINT",FACE,{"disambiguationData":[TD([[makeQuery(id+"F11.imprint","IMPRINT",EDGE,{"derivedFrom":sQuery(id+"F11.wireOp",EDGE,"E22.1.18.0")}),1.0]])]});
            var Q5;
            Q5=makeQuery(id+"F11.imprint","IMPRINT",FACE,{"disambiguationData":[TD([[makeQuery(id+"F11.imprint","IMPRINT",EDGE,{"derivedFrom":sQuery(id+"F11.wireOp",EDGE,"E26.8.0")}),1.0]])]});
            var Q6;
            Q6=makeQuery(id+"F11.imprint","IMPRINT",FACE,{"disambiguationData":[TD([[makeQuery(id+"F11.imprint","IMPRINT",EDGE,{"derivedFrom":sQuery(id+"F11.wireOp",EDGE,"E22.1.17.0")}),1.0]])]});
            var Q7;
            Q7=makeQuery(id+"F11.imprint","IMPRINT",FACE,{"disambiguationData":[TD([[makeQuery(id+"F11.imprint","IMPRINT",EDGE,{"derivedFrom":sQuery(id+"F11.wireOp",EDGE,"E24.8.0")}),1.0]])]});
            var Q8;
            Q8=makeQuery(id+"F11.imprint","IMPRINT",FACE,{"disambiguationData":[TD([[makeQuery(id+"F11.imprint","IMPRINT",EDGE,{"derivedFrom":sQuery(id+"F11.wireOp",EDGE,"E28.7.0")}),1.0]])]});
            var Q9;
            Q9=makeQuery(id+"F11.imprint","IMPRINT",FACE,{"disambiguationData":[TD([[makeQuery(id+"F11.imprint","IMPRINT",EDGE,{"derivedFrom":sQuery(id+"F11.wireOp",EDGE,"E22.1.16.0")}),1.0]])]});
            var Q10;
            Q10=makeQuery(id+"F11.imprint","IMPRINT",FACE,{"disambiguationData":[TD([[makeQuery(id+"F11.imprint","IMPRINT",EDGE,{"derivedFrom":sQuery(id+"F11.wireOp",EDGE,"E14.1.15.0")}),1.0]])]});
            var Q11;
            Q11=makeQuery(id+"F11.imprint","IMPRINT",FACE,{"disambiguationData":[TD([[makeQuery(id+"F11.imprint","IMPRINT",EDGE,{"derivedFrom":sQuery(id+"F11.wireOp",EDGE,"E14.1.16.0")}),1.0]])]});
            var Q12;
            Q12=makeQuery(id+"F11.imprint","IMPRINT",FACE,{"disambiguationData":[TD([[makeQuery(id+"F11.imprint","IMPRINT",EDGE,{"derivedFrom":sQuery(id+"F11.wireOp",EDGE,"E14.1.17.0")}),1.0]])]});
            var Q13;
            Q13=makeQuery(id+"F11.imprint","IMPRINT",FACE,{"disambiguationData":[TD([[makeQuery(id+"F11.imprint","IMPRINT",EDGE,{"derivedFrom":sQuery(id+"F11.wireOp",EDGE,"E14.1.18.0")}),1.0]])]});
            var Q14;
            Q14=makeQuery(id+"F11.imprint","IMPRINT",FACE,{"disambiguationData":[TD([[makeQuery(id+"F11.imprint","IMPRINT",EDGE,{"derivedFrom":sQuery(id+"F11.wireOp",EDGE,"E15")}),1.0]])]});
            var Q15;
            {var subQ0=sQuery(id+"F11.wireOp",EDGE,"E18.1.11.0");var subQ1=makeQuery(id+"F11.imprint","INTERSECT",VERTEX,{"derivedFrom":[sQuery(id+"F11.wireOp",EDGE,"E8.1"),subQ0]});Q15=makeQuery(id+"F11.imprint","IMPRINT",FACE,{"disambiguationData":[TD([[makeQuery(id+"F11.imprint","IMPRINT",EDGE,{"disambiguationData":[TD([[subQ1,-1.0]])],"derivedFrom":subQ0}),1.0]])]});}
            var Q16;
            Q16=makeQuery(id+"F11.imprint","IMPRINT",FACE,{"disambiguationData":[TD([[makeQuery(id+"F11.imprint","IMPRINT",EDGE,{"derivedFrom":sQuery(id+"F11.wireOp",EDGE,"E17.1.10.0")}),1.0]])]});
            var Q17;
            Q17=makeQuery(id+"F11.imprint","IMPRINT",FACE,{"disambiguationData":[TD([[makeQuery(id+"F11.imprint","IMPRINT",EDGE,{"derivedFrom":sQuery(id+"F11.wireOp",EDGE,"E14.1.14.0")}),1.0]])]});
            var Q18;
            {var subQ0=sQuery(id+"F11.wireOp",EDGE,"E16.9.0");var subQ1=makeQuery(id+"F11.imprint","INTERSECT",VERTEX,{"derivedFrom":[sQuery(id+"F11.wireOp",EDGE,"E8.2"),subQ0]});Q18=makeQuery(id+"F11.imprint","IMPRINT",FACE,{"disambiguationData":[TD([[makeQuery(id+"F11.imprint","IMPRINT",EDGE,{"disambiguationData":[TD([[subQ1,-1.0]])],"derivedFrom":subQ0}),1.0]])]});}
            var Q19;
            Q19=makeQuery(id+"F11.imprint","IMPRINT",FACE,{"disambiguationData":[TD([[makeQuery(id+"F11.imprint","IMPRINT",EDGE,{"derivedFrom":sQuery(id+"F11.wireOp",EDGE,"E13.1.13.0")}),1.0]])]});
            var Q20;
            Q20=makeQuery(id+"F11.imprint","IMPRINT",FACE,{"disambiguationData":[TD([[makeQuery(id+"F11.imprint","IMPRINT",EDGE,{"derivedFrom":sQuery(id+"F11.wireOp",EDGE,"E26.7.0")}),1.0]])]});
            var Q21;
            Q21=makeQuery(id+"F11.imprint","IMPRINT",FACE,{"disambiguationData":[TD([[makeQuery(id+"F11.imprint","IMPRINT",EDGE,{"derivedFrom":sQuery(id+"F11.wireOp",EDGE,"E22.1.15.0")}),1.0]])]});
            var Q22;
            Q22=makeQuery(id+"F11.imprint","IMPRINT",FACE,{"disambiguationData":[TD([[makeQuery(id+"F11.imprint","IMPRINT",EDGE,{"derivedFrom":sQuery(id+"F11.wireOp",EDGE,"E24.7.0")}),1.0]])]});
            var Q23;
            Q23=makeQuery(id+"F11.imprint","IMPRINT",FACE,{"disambiguationData":[TD([[makeQuery(id+"F11.imprint","IMPRINT",EDGE,{"derivedFrom":sQuery(id+"F11.wireOp",EDGE,"E14.1.19.0")}),1.0]])]});
            var Q24;
            Q24=makeQuery(id+"F11.imprint","IMPRINT",FACE,{"disambiguationData":[TD([[makeQuery(id+"F11.imprint","IMPRINT",EDGE,{"derivedFrom":sQuery(id+"F11.wireOp",EDGE,"E19")}),1.0]])]});
            var Q25;
            {var subQ0=sQuery(id+"F11.wireOp",EDGE,"E16.1.0");var subQ1=makeQuery(id+"F11.imprint","INTERSECT",VERTEX,{"derivedFrom":[sQuery(id+"F11.wireOp",EDGE,"E8.0"),subQ0]});Q25=makeQuery(id+"F11.imprint","IMPRINT",FACE,{"disambiguationData":[TD([[makeQuery(id+"F11.imprint","IMPRINT",EDGE,{"disambiguationData":[TD([[subQ1,-1.0]])],"derivedFrom":subQ0}),1.0]])]});}
            var Q26;
            Q26=makeQuery(id+"F11.imprint","IMPRINT",FACE,{"disambiguationData":[TD([[makeQuery(id+"F11.imprint","IMPRINT",EDGE,{"derivedFrom":sQuery(id+"F11.wireOp",EDGE,"E28.9.0")}),1.0]])]});
            var Q27;
            Q27=makeQuery(id+"F11.imprint","IMPRINT",FACE,{"disambiguationData":[TD([[makeQuery(id+"F11.imprint","IMPRINT",EDGE,{"derivedFrom":sQuery(id+"F11.wireOp",EDGE,"E23")}),1.0]])]});
            var Q28;
            Q28=makeQuery(id+"F11.imprint","IMPRINT",FACE,{"disambiguationData":[TD([[makeQuery(id+"F11.imprint","IMPRINT",EDGE,{"derivedFrom":sQuery(id+"F11.wireOp",EDGE,"E21")}),1.0]])]});
            var Q29;
            Q29=makeQuery(id+"F11.imprint","IMPRINT",FACE,{"disambiguationData":[TD([[makeQuery(id+"F11.imprint","IMPRINT",EDGE,{"derivedFrom":sQuery(id+"F11.wireOp",EDGE,"E9")}),1.0]])]});
            var Q30;
            Q30=makeQuery(id+"F11.imprint","IMPRINT",FACE,{"disambiguationData":[TD([[makeQuery(id+"F11.imprint","IMPRINT",EDGE,{"derivedFrom":sQuery(id+"F11.wireOp",EDGE,"E25")}),1.0]])]});
            var Q31;
            Q31=makeQuery(id+"F11.imprint","IMPRINT",FACE,{"disambiguationData":[TD([[makeQuery(id+"F11.imprint","IMPRINT",EDGE,{"derivedFrom":sQuery(id+"F11.wireOp",EDGE,"E20.2.0")}),1.0]])]});
            var Q32;
            Q32=makeQuery(id+"F11.imprint","IMPRINT",FACE,{"disambiguationData":[TD([[makeQuery(id+"F11.imprint","IMPRINT",EDGE,{"derivedFrom":sQuery(id+"F11.wireOp",EDGE,"E27")}),1.0]])]});
            var Q33;
            Q33=makeQuery(id+"F11.imprint","IMPRINT",FACE,{"disambiguationData":[TD([[makeQuery(id+"F11.imprint","IMPRINT",EDGE,{"derivedFrom":sQuery(id+"F11.wireOp",EDGE,"E16.2.0")}),1.0]])]});
            var Q34;
            Q34=makeQuery(id+"F11.imprint","IMPRINT",FACE,{"disambiguationData":[TD([[makeQuery(id+"F11.imprint","IMPRINT",EDGE,{"derivedFrom":sQuery(id+"F11.wireOp",EDGE,"E10.1.0")}),1.0]])]});
            var Q35;
            Q35=makeQuery(id+"F11.imprint","IMPRINT",FACE,{"disambiguationData":[TD([[makeQuery(id+"F11.imprint","IMPRINT",EDGE,{"derivedFrom":sQuery(id+"F11.wireOp",EDGE,"E20.3.0")}),1.0]])]});
            var Q36;
            Q36=makeQuery(id+"F11.imprint","IMPRINT",FACE,{"disambiguationData":[TD([[makeQuery(id+"F11.imprint","IMPRINT",EDGE,{"derivedFrom":sQuery(id+"F11.wireOp",EDGE,"E10.2.0")}),1.0]])]});
            var Q37;
            {var subQ0=sQuery(id+"F11.wireOp",EDGE,"E16.3.0");var subQ1=makeQuery(id+"F11.imprint","INTERSECT",VERTEX,{"derivedFrom":[sQuery(id+"F11.wireOp",EDGE,"E8.0"),subQ0]});Q37=makeQuery(id+"F11.imprint","IMPRINT",FACE,{"disambiguationData":[TD([[makeQuery(id+"F11.imprint","IMPRINT",EDGE,{"disambiguationData":[TD([[subQ1,1.0]])],"derivedFrom":subQ0}),1.0]])]});}
            var Q38;
            Q38=makeQuery(id+"F11.imprint","IMPRINT",FACE,{"disambiguationData":[TD([[makeQuery(id+"F11.imprint","IMPRINT",EDGE,{"derivedFrom":sQuery(id+"F11.wireOp",EDGE,"E24.1.0")}),1.0]])]});
            var Q39;
            Q39=makeQuery(id+"F11.imprint","IMPRINT",FACE,{"disambiguationData":[TD([[makeQuery(id+"F11.imprint","IMPRINT",EDGE,{"derivedFrom":sQuery(id+"F11.wireOp",EDGE,"E26.1.0")}),1.0]])]});
            var Q40;
            Q40=makeQuery(id+"F11.imprint","IMPRINT",FACE,{"disambiguationData":[TD([[makeQuery(id+"F11.imprint","IMPRINT",EDGE,{"derivedFrom":sQuery(id+"F11.wireOp",EDGE,"E28.1.0")}),1.0]])]});
            var Q41;
            Q41=makeQuery(id+"F11.imprint","IMPRINT",FACE,{"disambiguationData":[TD([[makeQuery(id+"F11.imprint","IMPRINT",EDGE,{"derivedFrom":sQuery(id+"F11.wireOp",EDGE,"E20.4.0")}),1.0]])]});
            var Q42;
            Q42=makeQuery(id+"F11.imprint","IMPRINT",FACE,{"disambiguationData":[TD([[makeQuery(id+"F11.imprint","IMPRINT",EDGE,{"derivedFrom":sQuery(id+"F11.wireOp",EDGE,"E11.1.3.0")}),1.0]])]});
            var Q43;
            Q43=makeQuery(id+"F11.imprint","IMPRINT",FACE,{"disambiguationData":[TD([[makeQuery(id+"F11.imprint","IMPRINT",EDGE,{"derivedFrom":sQuery(id+"F11.wireOp",EDGE,"E20.5.0")}),1.0]])]});
            var Q44;
            Q44=makeQuery(id+"F11.imprint","IMPRINT",FACE,{"disambiguationData":[TD([[makeQuery(id+"F11.imprint","IMPRINT",EDGE,{"derivedFrom":sQuery(id+"F11.wireOp",EDGE,"E26.2.0")}),1.0]])]});
            var Q45;
            Q45=makeQuery(id+"F11.imprint","IMPRINT",FACE,{"disambiguationData":[TD([[makeQuery(id+"F11.imprint","IMPRINT",EDGE,{"derivedFrom":sQuery(id+"F11.wireOp",EDGE,"E24.2.0")}),1.0]])]});
            var Q46;
            Q46=makeQuery(id+"F11.imprint","IMPRINT",FACE,{"disambiguationData":[TD([[makeQuery(id+"F11.imprint","IMPRINT",EDGE,{"derivedFrom":sQuery(id+"F11.wireOp",EDGE,"E11.1.4.0")}),1.0]])]});
            var Q47;
            Q47=makeQuery(id+"F11.imprint","IMPRINT",FACE,{"disambiguationData":[TD([[makeQuery(id+"F11.imprint","IMPRINT",EDGE,{"derivedFrom":sQuery(id+"F11.wireOp",EDGE,"E16.4.0")}),1.0]])]});
            var Q48;
            Q48=makeQuery(id+"F11.imprint","IMPRINT",FACE,{"disambiguationData":[TD([[makeQuery(id+"F11.imprint","IMPRINT",EDGE,{"derivedFrom":sQuery(id+"F11.wireOp",EDGE,"E20.6.0")}),1.0]])]});
            var Q49;
            Q49=makeQuery(id+"F11.imprint","IMPRINT",FACE,{"disambiguationData":[TD([[makeQuery(id+"F11.imprint","IMPRINT",EDGE,{"derivedFrom":sQuery(id+"F11.wireOp",EDGE,"E11.1.5.0")}),1.0]])]});
            var Q50;
            {var subQ0=sQuery(id+"F11.wireOp",EDGE,"E16.5.0");var subQ1=makeQuery(id+"F11.imprint","INTERSECT",VERTEX,{"derivedFrom":[sQuery(id+"F11.wireOp",EDGE,"E8.4"),subQ0]});Q50=makeQuery(id+"F11.imprint","IMPRINT",FACE,{"disambiguationData":[TD([[makeQuery(id+"F11.imprint","IMPRINT",EDGE,{"disambiguationData":[TD([[subQ1,-1.0]])],"derivedFrom":subQ0}),1.0]])]});}
            var Q51;
            Q51=makeQuery(id+"F11.imprint","IMPRINT",FACE,{"disambiguationData":[TD([[makeQuery(id+"F11.imprint","IMPRINT",EDGE,{"derivedFrom":sQuery(id+"F11.wireOp",EDGE,"E11.1.6.0")}),1.0]])]});
            var Q52;
            Q52=makeQuery(id+"F11.imprint","IMPRINT",FACE,{"disambiguationData":[TD([[makeQuery(id+"F11.imprint","IMPRINT",EDGE,{"derivedFrom":sQuery(id+"F11.wireOp",EDGE,"E20.7.0")}),1.0]])]});
            var Q53;
            Q53=makeQuery(id+"F11.imprint","IMPRINT",FACE,{"disambiguationData":[TD([[makeQuery(id+"F11.imprint","IMPRINT",EDGE,{"derivedFrom":sQuery(id+"F11.wireOp",EDGE,"E24.3.0")}),1.0]])]});
            var Q54;
            Q54=makeQuery(id+"F11.imprint","IMPRINT",FACE,{"disambiguationData":[TD([[makeQuery(id+"F11.imprint","IMPRINT",EDGE,{"derivedFrom":sQuery(id+"F11.wireOp",EDGE,"E28.2.0")}),1.0]])]});
            var Q55;
            Q55=makeQuery(id+"F11.imprint","IMPRINT",FACE,{"disambiguationData":[TD([[makeQuery(id+"F11.imprint","IMPRINT",EDGE,{"derivedFrom":sQuery(id+"F11.wireOp",EDGE,"E26.3.0")}),1.0]])]});
            var Q56;
            Q56=makeQuery(id+"F11.imprint","IMPRINT",FACE,{"disambiguationData":[TD([[makeQuery(id+"F11.imprint","IMPRINT",EDGE,{"derivedFrom":sQuery(id+"F11.wireOp",EDGE,"E28.3.0")}),1.0]])]});
            var Q57;
            Q57=makeQuery(id+"F11.imprint","IMPRINT",FACE,{"disambiguationData":[TD([[makeQuery(id+"F11.imprint","IMPRINT",EDGE,{"derivedFrom":sQuery(id+"F11.wireOp",EDGE,"E20.8.0")}),1.0]])]});
            var Q58;
            Q58=makeQuery(id+"F11.imprint","IMPRINT",FACE,{"disambiguationData":[TD([[makeQuery(id+"F11.imprint","IMPRINT",EDGE,{"derivedFrom":sQuery(id+"F11.wireOp",EDGE,"E11.1.7.0")}),1.0]])]});
            var Q59;
            Q59=makeQuery(id+"F11.imprint","IMPRINT",FACE,{"disambiguationData":[TD([[makeQuery(id+"F11.imprint","IMPRINT",EDGE,{"derivedFrom":sQuery(id+"F11.wireOp",EDGE,"E20.9.0")}),1.0]])]});
            var Q60;
            Q60=makeQuery(id+"F11.imprint","IMPRINT",FACE,{"disambiguationData":[TD([[makeQuery(id+"F11.imprint","IMPRINT",EDGE,{"derivedFrom":sQuery(id+"F11.wireOp",EDGE,"E26.4.0")}),1.0]])]});
            var Q61;
            Q61=makeQuery(id+"F11.imprint","IMPRINT",FACE,{"disambiguationData":[TD([[makeQuery(id+"F11.imprint","IMPRINT",EDGE,{"derivedFrom":sQuery(id+"F11.wireOp",EDGE,"E24.4.0")}),1.0]])]});
            var Q62;
            Q62=makeQuery(id+"F11.imprint","IMPRINT",FACE,{"disambiguationData":[TD([[makeQuery(id+"F11.imprint","IMPRINT",EDGE,{"derivedFrom":sQuery(id+"F11.wireOp",EDGE,"E11.1.8.0")}),1.0]])]});
            var Q63;
            Q63=makeQuery(id+"F11.imprint","IMPRINT",FACE,{"disambiguationData":[TD([[makeQuery(id+"F11.imprint","IMPRINT",EDGE,{"derivedFrom":sQuery(id+"F11.wireOp",EDGE,"E16.6.0")}),1.0]])]});
            var Q64;
            Q64=makeQuery(id+"F11.imprint","IMPRINT",FACE,{"disambiguationData":[TD([[makeQuery(id+"F11.imprint","IMPRINT",EDGE,{"derivedFrom":sQuery(id+"F11.wireOp",EDGE,"E11.1.9.0")}),1.0]])]});
            var Q65;
            Q65=makeQuery(id+"F11.imprint","IMPRINT",FACE,{"disambiguationData":[TD([[makeQuery(id+"F11.imprint","IMPRINT",EDGE,{"derivedFrom":sQuery(id+"F11.wireOp",EDGE,"E22.1.10.0")}),1.0]])]});
            var Q66;
            Q66=makeQuery(id+"F11.imprint","IMPRINT",FACE,{"disambiguationData":[TD([[makeQuery(id+"F11.imprint","IMPRINT",EDGE,{"derivedFrom":sQuery(id+"F11.wireOp",EDGE,"E28.4.0")}),1.0]])]});
            var Q67;
            Q67=makeQuery(id+"F11.imprint","IMPRINT",FACE,{"disambiguationData":[TD([[makeQuery(id+"F11.imprint","IMPRINT",EDGE,{"derivedFrom":sQuery(id+"F11.wireOp",EDGE,"E24.5.0")}),1.0]])]});
            var Q68;
            Q68=makeQuery(id+"F11.imprint","IMPRINT",FACE,{"disambiguationData":[TD([[makeQuery(id+"F11.imprint","IMPRINT",EDGE,{"derivedFrom":sQuery(id+"F11.wireOp",EDGE,"E22.1.11.0")}),1.0]])]});
            var Q69;
            Q69=makeQuery(id+"F11.imprint","IMPRINT",FACE,{"disambiguationData":[TD([[makeQuery(id+"F11.imprint","IMPRINT",EDGE,{"derivedFrom":sQuery(id+"F11.wireOp",EDGE,"E26.5.0")}),1.0]])]});
            var Q70;
            Q70=makeQuery(id+"F11.imprint","IMPRINT",FACE,{"disambiguationData":[TD([[makeQuery(id+"F11.imprint","IMPRINT",EDGE,{"derivedFrom":sQuery(id+"F11.wireOp",EDGE,"E11.1.10.0")}),1.0]])]});
            var Q71;
            {var subQ0=sQuery(id+"F11.wireOp",EDGE,"E16.7.0");var subQ1=makeQuery(id+"F11.imprint","INTERSECT",VERTEX,{"derivedFrom":[sQuery(id+"F11.wireOp",EDGE,"E8.3"),subQ0]});Q71=makeQuery(id+"F11.imprint","IMPRINT",FACE,{"disambiguationData":[TD([[makeQuery(id+"F11.imprint","IMPRINT",EDGE,{"disambiguationData":[TD([[subQ1,-1.0]])],"derivedFrom":subQ0}),1.0]])]});}
            var Q72;
            Q72=makeQuery(id+"F11.imprint","IMPRINT",FACE,{"disambiguationData":[TD([[makeQuery(id+"F11.imprint","IMPRINT",EDGE,{"derivedFrom":sQuery(id+"F11.wireOp",EDGE,"E16.8.0")}),1.0]])]});
            var Q73;
            Q73=makeQuery(id+"F11.imprint","IMPRINT",FACE,{"disambiguationData":[TD([[makeQuery(id+"F11.imprint","IMPRINT",EDGE,{"derivedFrom":sQuery(id+"F11.wireOp",EDGE,"E11.1.11.0")}),1.0]])]});
            var Q74;
            Q74=makeQuery(id+"F11.imprint","IMPRINT",FACE,{"disambiguationData":[TD([[makeQuery(id+"F11.imprint","IMPRINT",EDGE,{"derivedFrom":sQuery(id+"F11.wireOp",EDGE,"E12.1.12.0")}),1.0]])]});
            var Q75;
            Q75=makeQuery(id+"F11.imprint","IMPRINT",FACE,{"disambiguationData":[TD([[makeQuery(id+"F11.imprint","IMPRINT",EDGE,{"derivedFrom":sQuery(id+"F11.wireOp",EDGE,"E22.1.14.0")}),1.0]])]});
            var Q76;
            Q76=makeQuery(id+"F11.imprint","IMPRINT",FACE,{"disambiguationData":[TD([[makeQuery(id+"F11.imprint","IMPRINT",EDGE,{"derivedFrom":sQuery(id+"F11.wireOp",EDGE,"E28.6.0")}),1.0]])]});
            var Q77;
            Q77=makeQuery(id+"F11.imprint","IMPRINT",FACE,{"disambiguationData":[TD([[makeQuery(id+"F11.imprint","IMPRINT",EDGE,{"derivedFrom":sQuery(id+"F11.wireOp",EDGE,"E22.1.13.0")}),1.0]])]});
            var Q78;
            Q78=makeQuery(id+"F11.imprint","IMPRINT",FACE,{"disambiguationData":[TD([[makeQuery(id+"F11.imprint","IMPRINT",EDGE,{"derivedFrom":sQuery(id+"F11.wireOp",EDGE,"E26.6.0")}),1.0]])]});
            var Q79;
            Q79=makeQuery(id+"F11.imprint","IMPRINT",FACE,{"disambiguationData":[TD([[makeQuery(id+"F11.imprint","IMPRINT",EDGE,{"derivedFrom":sQuery(id+"F11.wireOp",EDGE,"E24.6.0")}),1.0]])]});
            var Q80;
            Q80=makeQuery(id+"F11.imprint","IMPRINT",FACE,{"disambiguationData":[TD([[makeQuery(id+"F11.imprint","IMPRINT",EDGE,{"derivedFrom":sQuery(id+"F11.wireOp",EDGE,"E22.1.12.0")}),1.0]])]});
            var Q81;
            Q81=makeQuery(id+"F11.imprint","IMPRINT",FACE,{"disambiguationData":[TD([[makeQuery(id+"F11.imprint","IMPRINT",EDGE,{"derivedFrom":sQuery(id+"F11.wireOp",EDGE,"E28.5.0")}),1.0]])]});
            var Q82;
            Q82=makeQuery(id+"F8.opChamfer","BLEND_FACE",FACE,{"disambiguationData":[OSD([sQuery(id+"F6.wireOp",EDGE,"E6.top")])]});
            extrude(context, id + "F13", {"entities" : qUnion([Q0, Q1, Q2, Q3, Q4, Q5, Q6, Q7, Q8, Q9, Q10, Q11, Q12, Q13, Q14, Q15, Q16, Q17, Q18, Q19, Q20, Q21, Q22, Q23, Q24, Q25, Q26, Q27, Q28, Q29, Q30, Q31, Q32, Q33, Q34, Q35, Q36, Q37, Q38, Q39, Q40, Q41, Q42, Q43, Q44, Q45, Q46, Q47, Q48, Q49, Q50, Q51, Q52, Q53, Q54, Q55, Q56, Q57, Q58, Q59, Q60, Q61, Q62, Q63, Q64, Q65, Q66, Q67, Q68, Q69, Q70, Q71, Q72, Q73, Q74, Q75, Q76, Q77, Q78, Q79, Q80, Q81, Q82]), "operationType" : NewBodyOperationType.REMOVE, "depth" : 0.24 * mm, "offsetDistance" : 25 * mm});
        }
    });
